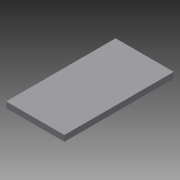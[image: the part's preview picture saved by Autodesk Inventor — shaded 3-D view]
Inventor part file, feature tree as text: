
AUTODESK INVENTOR PART (.ipt)
format: ipt  version: 2015 (Build 190159000, 159)  size: 65,536 bytes
history: native  units: in
note: dims shown in document units (in); Inventor stores cm internally (conversion verified against a paired STEP export)
features: extrude x1, sketch x1
ambient origin geometry x8: Origin, YZ Plane, XZ Plane, XY Plane, X Axis, Y Axis, Z Axis, Center Point
bodies: Solid1 (feature_tree)
feature tree (2):
  extrude  "Extrusion1"  [1 undecoded]
  sketch  "Sketch1"  dims[d0=0.1in d1=0.0in]
note: 1 required parameter value undecoded (feature->parameter linkage not recoverable at this tier; creation-order binding heuristic only, values carry confidence <= 0.55)
